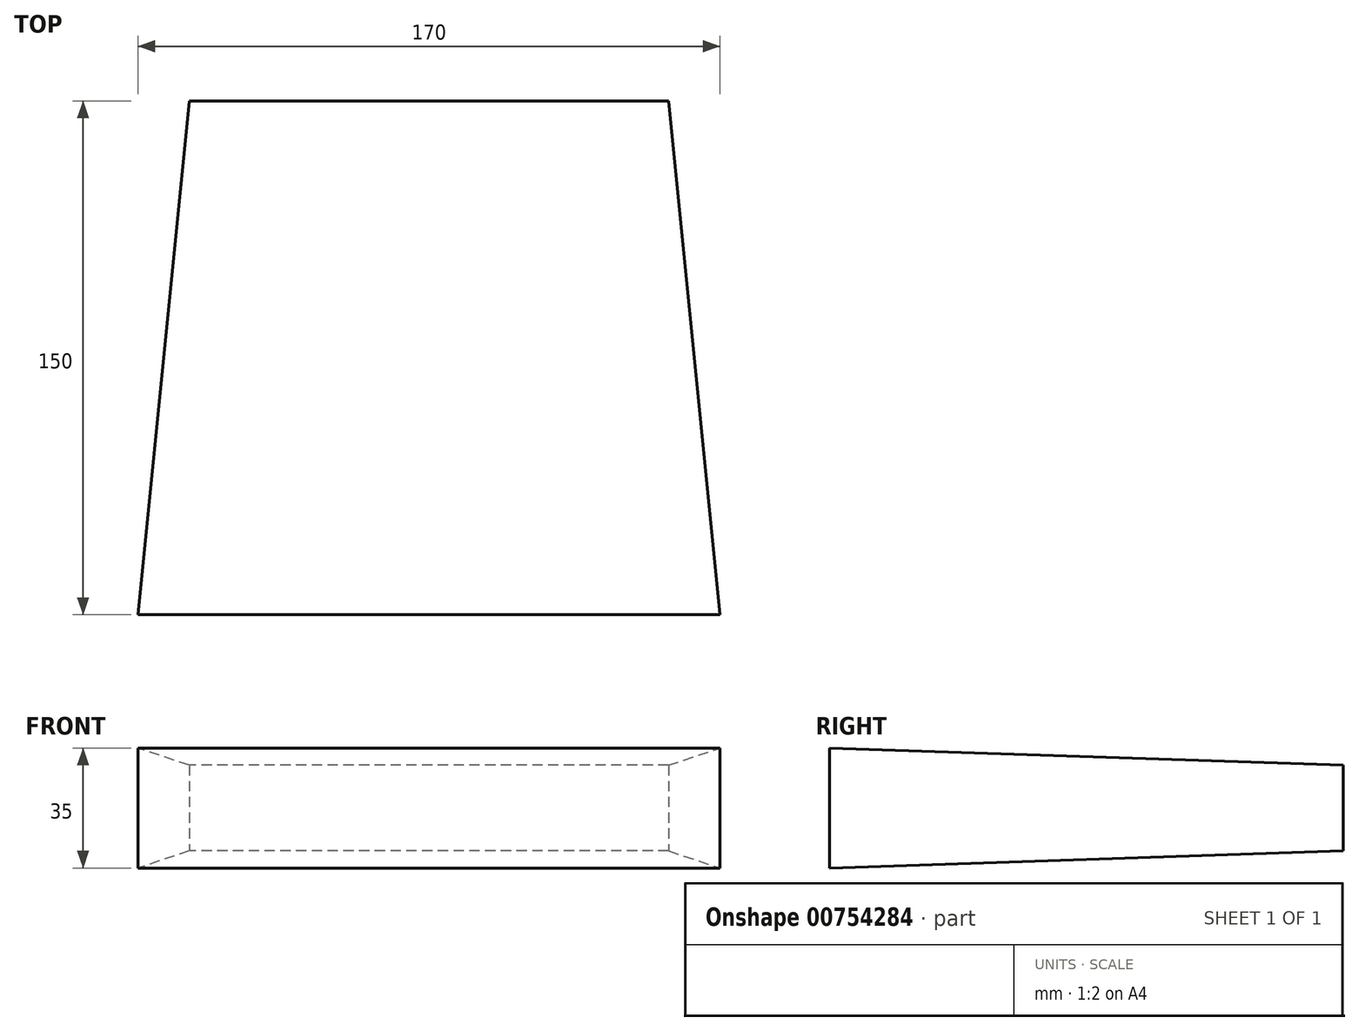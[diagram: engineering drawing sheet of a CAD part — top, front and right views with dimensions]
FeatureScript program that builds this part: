
annotation { "Feature Type Name" : "Feature", "Feature Type Description" : "" }
export const myFeature = defineFeature(function(context is Context, id is Id, definition is map)
    precondition{}
    {
        {
            var Q0;
            Q0=qCreatedBy(makeId("Front.planeOp"),FACE);
            var sketch = newSketch(context, id + "F0", { "sketchPlane" : qUnion([Q0])});
            skLineSegment(sketch, "E0.bottom", {"start": v(70, 12.5) * mm, "end": v(-70, 12.5) * mm});
            skLineSegment(sketch, "E0.top", {"start": v(70, -12.5) * mm, "end": v(-70, -12.5) * mm});
            skLineSegment(sketch, "E0.left", {"start": v(70, 12.5) * mm, "end": v(70, -12.5) * mm});
            skLineSegment(sketch, "E0.right", {"start": v(-70, 12.5) * mm, "end": v(-70, -12.5) * mm});
            skPoint(sketch, "E0.middle", {"position": v(0, 0) * mm});
            skSolve(sketch);
        }
        {
            var Q0;
            Q0=qCreatedBy(makeId("Front.planeOp"),FACE);
            cPlane(context, id + "F1", {"entities" : qUnion([Q0]), "cplaneType" : CPlaneType.OFFSET, "offset" : 150 * mm, "width" : 150 * mm, "height" : 150 * mm});
        }
        {
            var Q0;
            Q0=qCreatedBy(id+"F1.planeOp",FACE);
            var sketch = newSketch(context, id + "F2", { "sketchPlane" : qUnion([Q0])});
            skLineSegment(sketch, "E1.bottom", {"start": v(85, 17.5) * mm, "end": v(-85, 17.5) * mm});
            skLineSegment(sketch, "E1.top", {"start": v(85, -17.5) * mm, "end": v(-85, -17.5) * mm});
            skLineSegment(sketch, "E1.left", {"start": v(85, 17.5) * mm, "end": v(85, -17.5) * mm});
            skLineSegment(sketch, "E1.right", {"start": v(-85, 17.5) * mm, "end": v(-85, -17.5) * mm});
            skPoint(sketch, "E1.middle", {"position": v(0, 0) * mm});
            skSolve(sketch);
        }
        {
            var Q0;
            Q0=makeQuery(id+"F0.imprint","IMPRINT",FACE,{"disambiguationData":[TD([[makeQuery(id+"F0.imprint","IMPRINT",EDGE,{"derivedFrom":sQuery(id+"F0.wireOp",EDGE,"E0.bottom")}),1.0]])]});
            var Q1;
            Q1=makeQuery(id+"F2.imprint","IMPRINT",FACE,{"disambiguationData":[TD([[makeQuery(id+"F2.imprint","IMPRINT",EDGE,{"derivedFrom":sQuery(id+"F2.wireOp",EDGE,"E1.bottom")}),1.0]])]});
            loft(context, id + "F3", {"sheetProfilesArray" : [{ "sheetProfileEntities" : qUnion([Q0]) }, { "sheetProfileEntities" : qUnion([Q1]) }]});
        }
    });
